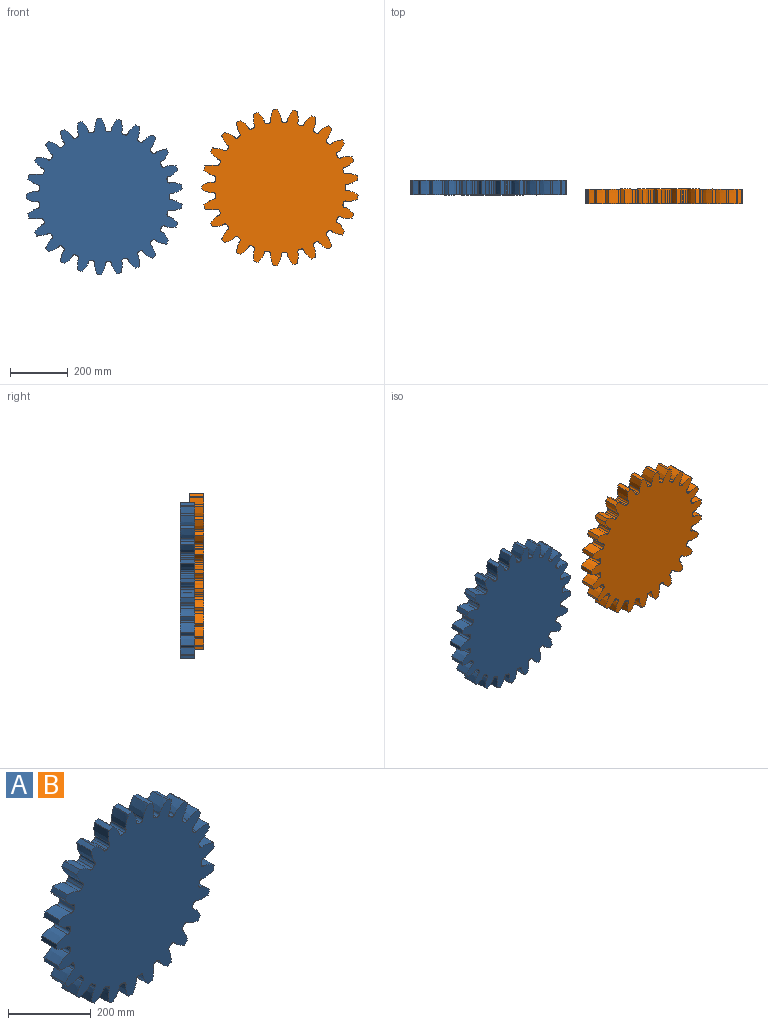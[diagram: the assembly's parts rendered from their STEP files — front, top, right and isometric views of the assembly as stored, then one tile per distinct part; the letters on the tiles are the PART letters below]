
ASSEMBLY  parts=2 mates=1
PART A: 152 faces, bbox 538.7x50x539.8 mm
  f0: extruded ~50x36.88mm, area 2027.4mm2, adj f99,f100,f101,f102
  f1: cylinder r=225mm len=50mm, axis (0,1,0), area 379.8mm2, adj f100,f101,f102,f103
  f2: extruded ~50x36.88mm, area 2027.4mm2, adj f3,f100,f101,f103
  f3: cylinder r=270mm len=50mm, axis (0,1,0), area 718.6mm2, adj f2,f4,f100,f101
  f4: extruded ~50x39.6mm, area 2027.4mm2, adj f3,f100,f101,f104
  f5: cylinder r=225mm len=50mm, axis (0,1,0), area 379.8mm2, adj f100,f101,f104,f105
  f6: extruded ~50x31.84mm, area 2027.4mm2, adj f7,f100,f101,f105
  f7: cylinder r=270mm len=50mm, axis (0,1,0), area 718.6mm2, adj f6,f8,f100,f101
  f8: extruded ~50x39.83mm, area 2027.4mm2, adj f7,f100,f101,f106
  f9: cylinder r=225mm len=50mm, axis (0,1,0), area 379.8mm2, adj f100,f101,f106,f107
  f10: extruded ~50x31.44mm, area 2027.4mm2, adj f11,f100,f101,f107
  f11: cylinder r=270mm len=50mm, axis (0,1,0), area 718.6mm2, adj f10,f12,f100,f101
  f12: extruded ~50x37.56mm, area 2027.4mm2, adj f11,f100,f101,f108
  f13: cylinder r=225mm len=50mm, axis (0,1,0), area 379.8mm2, adj f100,f101,f108,f109
  f14: extruded ~50x36.62mm, area 2027.4mm2, adj f15,f100,f101,f109
  f15: cylinder r=270mm len=50mm, axis (0,1,0), area 718.6mm2, adj f14,f16,f100,f101
  f16: extruded ~50x32.93mm, area 2027.4mm2, adj f15,f100,f101,f110
  f17: cylinder r=225mm len=50mm, axis (0,1,0), area 379.8mm2, adj f100,f101,f110,f111
  f18: extruded ~50x39.5mm, area 2027.4mm2, adj f19,f100,f101,f111
  f19: cylinder r=270mm len=50mm, axis (0,1,0), area 718.6mm2, adj f18,f20,f100,f101
  f20: extruded ~50x30.25mm, area 2027.4mm2, adj f19,f100,f101,f112
  f21: cylinder r=225mm len=50mm, axis (0,1,0), area 379.8mm2, adj f100,f101,f112,f113
  f22: extruded ~50x39.89mm, area 2027.4mm2, adj f23,f100,f101,f113
  f23: cylinder r=270mm len=50mm, axis (0,1,0), area 718.6mm2, adj f22,f24,f100,f101
  f24: extruded ~50x35.82mm, area 2027.4mm2, adj f23,f100,f101,f114
  f25: cylinder r=225mm len=50mm, axis (0,1,0), area 379.8mm2, adj f100,f101,f114,f115
  f26: extruded ~50x37.78mm, area 2027.4mm2, adj f27,f100,f101,f115
  f27: cylinder r=270mm len=50mm, axis (0,1,0), area 718.6mm2, adj f26,f28,f100,f101
  f28: extruded ~50x39.15mm, area 2027.4mm2, adj f27,f100,f101,f116
  f29: cylinder r=225mm len=50mm, axis (0,1,0), area 379.8mm2, adj f100,f101,f116,f117
  f30: extruded ~50x33.3mm, area 2027.4mm2, adj f31,f100,f101,f117
  f31: cylinder r=270mm len=50mm, axis (0,1,0), area 718.6mm2, adj f30,f32,f100,f101
  f32: extruded ~50x40.01mm, area 2027.4mm2, adj f31,f100,f101,f118
  f33: cylinder r=225mm len=50mm, axis (0,1,0), area 379.8mm2, adj f100,f101,f118,f119
  f34: extruded ~50x29.82mm, area 2027.4mm2, adj f35,f100,f101,f119
  f35: cylinder r=270mm len=50mm, axis (0,1,0), area 718.6mm2, adj f34,f36,f100,f101
  f36: extruded ~50x38.36mm, area 2027.4mm2, adj f35,f100,f101,f120
  f37: cylinder r=225mm len=50mm, axis (0,1,0), area 379.8mm2, adj f100,f101,f120,f121
  f38: extruded ~50x35.53mm, area 2027.4mm2, adj f39,f100,f101,f121
  f39: cylinder r=270mm len=50mm, axis (0,1,0), area 718.6mm2, adj f38,f40,f100,f101
  f40: extruded ~50x34.3mm, area 2027.4mm2, adj f39,f100,f101,f122
  f41: cylinder r=225mm len=50mm, axis (0,1,0), area 379.8mm2, adj f100,f101,f122,f123
  f42: extruded ~50x39mm, area 2027.4mm2, adj f43,f100,f101,f123
  f43: cylinder r=270mm len=50mm, axis (0,1,0), area 718.6mm2, adj f42,f44,f100,f101
  f44: extruded ~50x28.54mm, area 2027.4mm2, adj f43,f100,f101,f124
  f45: cylinder r=225mm len=50mm, axis (0,1,0), area 379.8mm2, adj f100,f101,f124,f125
  f46: extruded ~50x40.03mm, area 2027.4mm2, adj f47,f100,f101,f125
  f47: cylinder r=270mm len=50mm, axis (0,1,0), area 718.6mm2, adj f46,f48,f100,f101
  f48: extruded ~50x34.63mm, area 2027.4mm2, adj f47,f100,f101,f126
  f49: cylinder r=225mm len=50mm, axis (0,1,0), area 379.8mm2, adj f100,f101,f126,f127
  f50: extruded ~50x38.54mm, area 2027.4mm2, adj f51,f100,f101,f127
  f51: cylinder r=270mm len=50mm, axis (0,1,0), area 718.6mm2, adj f50,f52,f100,f101
  f52: extruded ~50x38.54mm, area 2027.4mm2, adj f51,f100,f101,f128
  f53: cylinder r=225mm len=50mm, axis (0,1,0), area 379.8mm2, adj f100,f101,f128,f129
  f54: extruded ~50x34.63mm, area 2027.4mm2, adj f55,f100,f101,f129
  f55: cylinder r=270mm len=50mm, axis (0,1,0), area 718.6mm2, adj f54,f56,f100,f101
  f56: extruded ~50x40.03mm, area 2027.4mm2, adj f55,f100,f101,f130
  f57: cylinder r=225mm len=50mm, axis (0,1,0), area 379.8mm2, adj f100,f101,f130,f131
  f58: extruded ~50x28.54mm, area 2027.4mm2, adj f59,f100,f101,f131
  f59: cylinder r=270mm len=50mm, axis (0,1,0), area 718.6mm2, adj f58,f60,f100,f101
  f60: extruded ~50x39mm, area 2027.4mm2, adj f59,f100,f101,f132
  f61: cylinder r=225mm len=50mm, axis (0,1,0), area 379.8mm2, adj f100,f101,f132,f133
  f62: extruded ~50x34.3mm, area 2027.4mm2, adj f63,f100,f101,f133
  f63: cylinder r=270mm len=50mm, axis (0,1,0), area 718.6mm2, adj f62,f64,f100,f101
  f64: extruded ~50x35.53mm, area 2027.4mm2, adj f63,f100,f101,f134
  f65: cylinder r=225mm len=50mm, axis (0,1,0), area 379.8mm2, adj f100,f101,f134,f135
  f66: extruded ~50x38.36mm, area 2027.4mm2, adj f67,f100,f101,f135
  f67: cylinder r=270mm len=50mm, axis (0,1,0), area 718.6mm2, adj f66,f68,f100,f101
  f68: extruded ~50x29.82mm, area 2027.4mm2, adj f67,f100,f101,f136
  f69: cylinder r=225mm len=50mm, axis (0,1,0), area 379.8mm2, adj f100,f101,f136,f137
  f70: extruded ~50x40.01mm, area 2027.4mm2, adj f71,f100,f101,f137
  f71: cylinder r=270mm len=50mm, axis (0,1,0), area 718.6mm2, adj f70,f72,f100,f101
  f72: extruded ~50x33.3mm, area 2027.4mm2, adj f71,f100,f101,f138
  f73: cylinder r=225mm len=50mm, axis (0,1,0), area 379.8mm2, adj f100,f101,f138,f139
  f74: extruded ~50x39.15mm, area 2027.4mm2, adj f75,f100,f101,f139
  f75: cylinder r=270mm len=50mm, axis (0,1,0), area 718.6mm2, adj f74,f76,f100,f101
  f76: extruded ~50x37.78mm, area 2027.4mm2, adj f75,f100,f101,f140
  f77: cylinder r=225mm len=50mm, axis (0,1,0), area 379.8mm2, adj f100,f101,f140,f141
  f78: extruded ~50x35.82mm, area 2027.4mm2, adj f79,f100,f101,f141
  f79: cylinder r=270mm len=50mm, axis (0,1,0), area 718.6mm2, adj f78,f80,f100,f101
  f80: extruded ~50x39.89mm, area 2027.4mm2, adj f79,f100,f101,f142
  f81: cylinder r=225mm len=50mm, axis (0,1,0), area 379.8mm2, adj f100,f101,f142,f143
  f82: extruded ~50x30.25mm, area 2027.4mm2, adj f83,f100,f101,f143
  f83: cylinder r=270mm len=50mm, axis (0,1,0), area 718.6mm2, adj f82,f84,f100,f101
  f84: extruded ~50x39.5mm, area 2027.4mm2, adj f83,f100,f101,f144
  f85: cylinder r=225mm len=50mm, axis (0,1,0), area 379.8mm2, adj f100,f101,f144,f145
  f86: extruded ~50x32.93mm, area 2027.4mm2, adj f87,f100,f101,f145
  f87: cylinder r=270mm len=50mm, axis (0,1,0), area 718.6mm2, adj f86,f88,f100,f101
  f88: extruded ~50x36.62mm, area 2027.4mm2, adj f87,f100,f101,f146
  f89: cylinder r=225mm len=50mm, axis (0,1,0), area 379.8mm2, adj f100,f101,f146,f147
  f90: extruded ~50x37.56mm, area 2027.4mm2, adj f91,f100,f101,f147
  f91: cylinder r=270mm len=50mm, axis (0,1,0), area 718.6mm2, adj f90,f92,f100,f101
  f92: extruded ~50x31.44mm, area 2027.4mm2, adj f91,f100,f101,f148
  f93: cylinder r=225mm len=50mm, axis (0,1,0), area 379.8mm2, adj f100,f101,f148,f149
  f94: extruded ~50x39.83mm, area 2027.4mm2, adj f95,f100,f101,f149
  f95: cylinder r=270mm len=50mm, axis (0,1,0), area 718.6mm2, adj f94,f96,f100,f101
  f96: extruded ~50x31.84mm, area 2027.4mm2, adj f95,f100,f101,f150
  f97: cylinder r=225mm len=50mm, axis (0,1,0), area 379.8mm2, adj f100,f101,f150,f151
  f98: extruded ~50x39.6mm, area 2027.4mm2, adj f99,f100,f101,f151
  f99: cylinder r=270mm len=50mm, axis (0,1,0), area 718.6mm2, adj f0,f98,f100,f101
  f100: plane 539.77x538.74mm, normal (0,-1,0), area 193394.3mm2, adj f0,f1,f2,f3,f4,f5,f6,f7
  f101: plane 539.77x538.74mm, normal (0,1,0), area 193394.3mm2, adj f0,f1,f2,f3,f4,f5,f6,f7
  f102: cylinder r=7.19mm len=50mm, axis (0,1,0), area 552.9mm2, adj f0,f1,f100,f101
  f103: cylinder r=7.19mm len=50mm, axis (0,1,0), area 552.9mm2, adj f1,f2,f100,f101
  f104: cylinder r=7.19mm len=50mm, axis (0,1,0), area 552.9mm2, adj f4,f5,f100,f101
  f105: cylinder r=7.19mm len=50mm, axis (0,1,0), area 552.9mm2, adj f5,f6,f100,f101
  f106: cylinder r=7.19mm len=50mm, axis (0,1,0), area 552.9mm2, adj f8,f9,f100,f101
  f107: cylinder r=7.19mm len=50mm, axis (0,1,0), area 552.9mm2, adj f9,f10,f100,f101
  f108: cylinder r=7.19mm len=50mm, axis (0,1,0), area 552.9mm2, adj f12,f13,f100,f101
  f109: cylinder r=7.19mm len=50mm, axis (0,1,0), area 552.9mm2, adj f13,f14,f100,f101
  f110: cylinder r=7.19mm len=50mm, axis (0,1,0), area 552.9mm2, adj f16,f17,f100,f101
  f111: cylinder r=7.19mm len=50mm, axis (0,1,0), area 552.9mm2, adj f17,f18,f100,f101
  f112: cylinder r=7.19mm len=50mm, axis (0,1,0), area 552.9mm2, adj f20,f21,f100,f101
  f113: cylinder r=7.19mm len=50mm, axis (0,1,0), area 552.9mm2, adj f21,f22,f100,f101
  f114: cylinder r=7.19mm len=50mm, axis (0,1,0), area 552.9mm2, adj f24,f25,f100,f101
  f115: cylinder r=7.19mm len=50mm, axis (0,1,0), area 552.9mm2, adj f25,f26,f100,f101
  f116: cylinder r=7.19mm len=50mm, axis (0,1,0), area 552.9mm2, adj f28,f29,f100,f101
  f117: cylinder r=7.19mm len=50mm, axis (0,1,0), area 552.9mm2, adj f29,f30,f100,f101
  f118: cylinder r=7.19mm len=50mm, axis (0,1,0), area 552.9mm2, adj f32,f33,f100,f101
  f119: cylinder r=7.19mm len=50mm, axis (0,1,0), area 552.9mm2, adj f33,f34,f100,f101
  f120: cylinder r=7.19mm len=50mm, axis (0,1,0), area 552.9mm2, adj f36,f37,f100,f101
  f121: cylinder r=7.19mm len=50mm, axis (0,1,0), area 552.9mm2, adj f37,f38,f100,f101
  f122: cylinder r=7.19mm len=50mm, axis (0,1,0), area 552.9mm2, adj f40,f41,f100,f101
  f123: cylinder r=7.19mm len=50mm, axis (0,1,0), area 552.9mm2, adj f41,f42,f100,f101
  f124: cylinder r=7.19mm len=50mm, axis (0,1,0), area 552.9mm2, adj f44,f45,f100,f101
  f125: cylinder r=7.19mm len=50mm, axis (0,1,0), area 552.9mm2, adj f45,f46,f100,f101
  f126: cylinder r=7.19mm len=50mm, axis (0,1,0), area 552.9mm2, adj f48,f49,f100,f101
  f127: cylinder r=7.19mm len=50mm, axis (0,1,0), area 552.9mm2, adj f49,f50,f100,f101
  f128: cylinder r=7.19mm len=50mm, axis (0,1,0), area 552.9mm2, adj f52,f53,f100,f101
  f129: cylinder r=7.19mm len=50mm, axis (0,1,0), area 552.9mm2, adj f53,f54,f100,f101
  f130: cylinder r=7.19mm len=50mm, axis (0,1,0), area 552.9mm2, adj f56,f57,f100,f101
  f131: cylinder r=7.19mm len=50mm, axis (0,1,0), area 552.9mm2, adj f57,f58,f100,f101
  f132: cylinder r=7.19mm len=50mm, axis (0,1,0), area 552.9mm2, adj f60,f61,f100,f101
  f133: cylinder r=7.19mm len=50mm, axis (0,1,0), area 552.9mm2, adj f61,f62,f100,f101
  f134: cylinder r=7.19mm len=50mm, axis (0,1,0), area 552.9mm2, adj f64,f65,f100,f101
  f135: cylinder r=7.19mm len=50mm, axis (0,1,0), area 552.9mm2, adj f65,f66,f100,f101
  f136: cylinder r=7.19mm len=50mm, axis (0,1,0), area 552.9mm2, adj f68,f69,f100,f101
  f137: cylinder r=7.19mm len=50mm, axis (0,1,0), area 552.9mm2, adj f69,f70,f100,f101
  f138: cylinder r=7.19mm len=50mm, axis (0,1,0), area 552.9mm2, adj f72,f73,f100,f101
  f139: cylinder r=7.19mm len=50mm, axis (0,1,0), area 552.9mm2, adj f73,f74,f100,f101
  f140: cylinder r=7.19mm len=50mm, axis (0,1,0), area 552.9mm2, adj f76,f77,f100,f101
  f141: cylinder r=7.19mm len=50mm, axis (0,1,0), area 552.9mm2, adj f77,f78,f100,f101
  f142: cylinder r=7.19mm len=50mm, axis (0,1,0), area 552.9mm2, adj f80,f81,f100,f101
  f143: cylinder r=7.19mm len=50mm, axis (0,1,0), area 552.9mm2, adj f81,f82,f100,f101
  f144: cylinder r=7.19mm len=50mm, axis (0,1,0), area 552.9mm2, adj f84,f85,f100,f101
  f145: cylinder r=7.19mm len=50mm, axis (0,1,0), area 552.9mm2, adj f85,f86,f100,f101
  f146: cylinder r=7.19mm len=50mm, axis (0,1,0), area 552.9mm2, adj f88,f89,f100,f101
  f147: cylinder r=7.19mm len=50mm, axis (0,1,0), area 552.9mm2, adj f89,f90,f100,f101
  f148: cylinder r=7.19mm len=50mm, axis (0,1,0), area 552.9mm2, adj f92,f93,f100,f101
  f149: cylinder r=7.19mm len=50mm, axis (0,1,0), area 552.9mm2, adj f93,f94,f100,f101
  f150: cylinder r=7.19mm len=50mm, axis (0,1,0), area 552.9mm2, adj f96,f97,f100,f101
  f151: cylinder r=7.19mm len=50mm, axis (0,1,0), area 552.9mm2, adj f97,f98,f100,f101
PART B: same geometry as A
PLACE A t=(143.49,296.76,32.99)mm
PLACE B t=(751.09,266.68,64.49)mm
MATE parallel A.f3 <-> B.f3  axis (0,-1,0) through (143.49,246.76,32.99)mm
